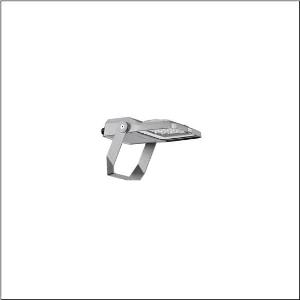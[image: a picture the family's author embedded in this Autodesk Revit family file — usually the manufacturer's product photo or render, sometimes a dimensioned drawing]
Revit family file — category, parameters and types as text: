
# Revit family: floodlight_fl_21_iq_micro___rs12_5xa7762a1b1a_c11c
name_source: partatom
category: Lighting Fixtures
units: mm (PartAtom-declared; Revit-internal decimal feet)

## family parameters
Cut with Voids When Loaded = No
Host = Face
Light Source = No
Part Type = Normal
Room Calculation Point = No
Round Connector Dimension = Use Diameter
Shared = No

## types (1)
- --- (1 x LED, 2560 lm, 23.1 W, 2200K)
    Apparent Load = 23 VA
    CIE Flux Codes = 79 92 99 100 100
    Color Rendering = 70
    Color Temperature = 2200K
    Default Elevation = 1800 mm
    Description = Floodlight FL 21 iQ micro, floodlight, primary light control with lens, of PMMA, primary optical cover: protective disc, of toughened safety glass, transparent, light distribution: RS12, light emission: direct distribution, installation type: surface-mounted, lamps: LED, High Power LED, rated values: 2.560lm | 23,1W | 110,8lm/W (begin service life); end service life: 2.560lm | 23,8W; at 50% lumin. flux: 1.280lm | 10,9W | 117,4lm/W, colour temperature: 2200K, colour rendering: CRI > 70, light colour: 722, light setting 1 begin service life: 100% | 2.560lm | 23,1W | 110,8lm/W | 2.200K, light setting 1 end service life: 23,8W, further light settings possible, control: Auto-Match, Temp-Guard, Night-Set, Smart-Wire, Desk-Remote (wireless, voltage-free reading and setting of iQ features in the workshop via application-optimized NFC function/RFID function), optimised constant luminous flux control (CLO 2.0), Street-Remote, pre-setting: linear dimming characteristic, with terminal, 6-pole, mains connection: 220..240V, AC, 50/60Hz, luminaire housing, of diecast aluminium, powder-coated, SITECO metallic grey (DB 702S), corrosivity category C5 mid according to DIN EN ISO 12944suitable for swimming poolschlorine-resistant, sealing non-destructively replaceable, mounting bracket, of steel, galvanised, powder-coated, SITECO metallic grey (DB 702S), protection rating (complete): IP66, insulation class (complete): insulation class II (safety insulation), certification: CE, ENEC, VDE, protection symbol: D, impact resistance: IK07, permissible operating ambient temperature: -40..+40°C, permissible operating ambient temperature for outdoor applications: -40..+50°C, standard: DIN EN 12944, LABS conformity tested according to VDMA 24364:2018-05, packaging unit: 1 piece

Light Distribution: RS12
    Height = 65 mm
    Lamp = 1 x LED
    Lamp Light Flux = 2560 lm
    Lamp Power = 23.1 W
    Lamp count = 1
    Length = 312 mm
    Luminous efficacy = 111 lm/W
    Manufacturer = Siteco
    ModVariant = No
    Model = 5XA7762A1B1A
    Mounting Place = Pole
    Mounting Type = Pole annexe
    Number of Poles = 1
    OnlyDefault = Yes
    Power Factor = 1
    Product Name = Floodlight FL 21 iQ micro | RS12
    Product group = floodlight | pylon annexe
    ProductGroupID = 6201
    Protection Class = Protection class II
    Protection Degree = IP 66
    RLX_Detail_Level = 1
    RLX_Emergency_Light_Flux = 0 lm
    RLX_Emergency_Type = 0
    RLX_Emergency_Type_DB = No
    RlxData = <blob elided: 75245 chars, md5=4c2d3474>
    Socket = socket
    Standby Power = 0 W
    System Light Flux = 2560 lm
    System Power = 23 W
    Type Comments = factory setting: luminous flux: 100 % | dim-lin: 254 | 455 mA
    Type Image = l_1006880.jpg
    URL = http://relux.com
    VarID = @adj_181341
    Voltage = 0 V
    Weight = 0.00 kg
    Width = 230 mm

## geometry (parser evidence)
native form markers: Blend x4, Sweep x13
no freeform markers — native parametric forms only
